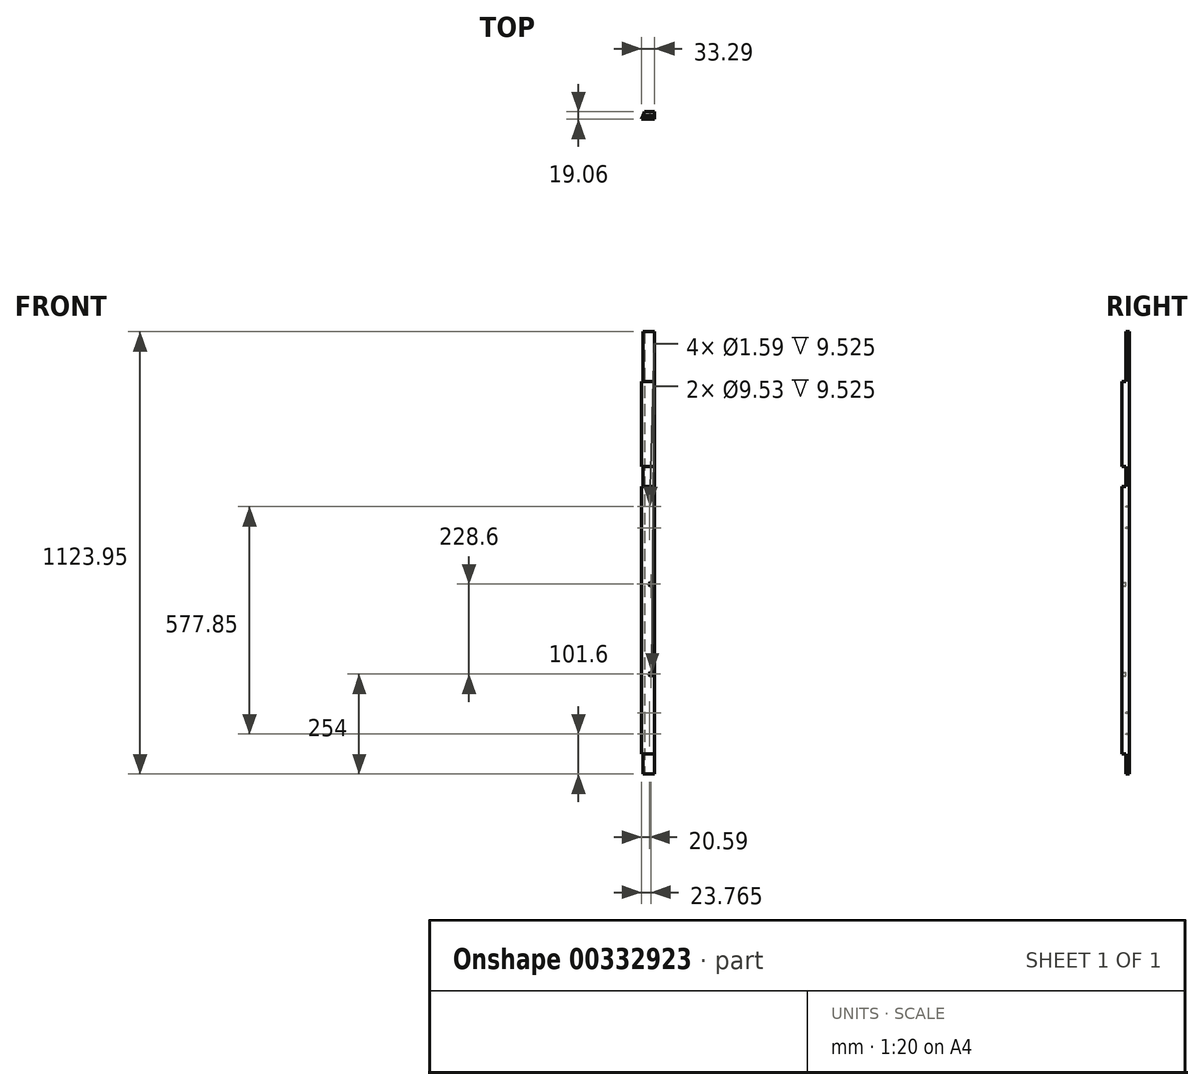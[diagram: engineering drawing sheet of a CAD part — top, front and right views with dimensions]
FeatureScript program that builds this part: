
annotation { "Feature Type Name" : "Feature", "Feature Type Description" : "" }
export const myFeature = defineFeature(function(context is Context, id is Id, definition is map)
    precondition{}
    {
        {
            var Q0;
            Q0=qCreatedBy(makeId("Top.planeOp"),FACE);
            var sketch = newSketch(context, id + "F0", { "sketchPlane" : qUnion([Q0])});
            skLineSegment(sketch, "E0.bottom", {"start": v(25.4, 9.53) * mm, "end": v(0, 9.53) * mm});
            skLineSegment(sketch, "E0.top", {"start": v(25.4, -9.53) * mm, "end": v(-7.9, -9.53) * mm});
            skLineSegment(sketch, "E0.left", {"start": v(25.4, 9.53) * mm, "end": v(25.4, -9.52) * mm});
            skPoint(sketch, "E0.middle", {"position": v(0, 0) * mm});
            skLineSegment(sketch, "E1", {"start": v(0, 9.53) * mm, "end": v(-7.9, -9.52) * mm});
            skPoint(sketch, "E0.right.end.orphan", {"position": v(-25.4, -9.53) * mm});
            skPoint(sketch, "E2.orphan", {"position": v(-25.4, 9.53) * mm});
            skSolve(sketch);
        }
        {
            var Q0;
            Q0=makeQuery(id+"F0.imprint","IMPRINT",FACE,{"disambiguationData":[TD([[makeQuery(id+"F0.imprint","IMPRINT",EDGE,{"derivedFrom":sQuery(id+"F0.wireOp",EDGE,"E0.bottom")}),1.0]])]});
            extrude(context, id + "F1", {"entities" : qUnion([Q0]), "depth" : 1123.95 * mm});
        }
        {
            var Q0;
            Q0=qCreatedBy(makeId("Front.planeOp"),FACE);
            var sketch = newSketch(context, id + "F2", { "sketchPlane" : qUnion([Q0])});
            skLineSegment(sketch, "E3.bottom", {"start": v(-38.77, 0) * mm, "end": v(83.66, 0) * mm});
            skLineSegment(sketch, "E3.top", {"start": v(-38.77, 50.8) * mm, "end": v(83.66, 50.8) * mm});
            skLineSegment(sketch, "E3.left", {"start": v(-38.77, 0) * mm, "end": v(-38.77, 50.8) * mm});
            skLineSegment(sketch, "E3.right", {"start": v(83.66, 0) * mm, "end": v(83.66, 50.8) * mm});
            skLineSegment(sketch, "E4.bottom", {"start": v(-44.21, 730.25) * mm, "end": v(49.65, 730.25) * mm});
            skLineSegment(sketch, "E4.top", {"start": v(-44.21, 781.05) * mm, "end": v(49.65, 781.05) * mm});
            skLineSegment(sketch, "E4.left", {"start": v(-44.21, 730.25) * mm, "end": v(-44.21, 781.05) * mm});
            skLineSegment(sketch, "E4.right", {"start": v(49.65, 730.25) * mm, "end": v(49.65, 781.05) * mm});
            skLineSegment(sketch, "E5.bottom", {"start": v(-210.36, 996.95) * mm, "end": v(132.8, 996.95) * mm});
            skLineSegment(sketch, "E5.top", {"start": v(-210.36, 1123.95) * mm, "end": v(132.8, 1123.95) * mm});
            skLineSegment(sketch, "E5.left", {"start": v(-210.36, 996.95) * mm, "end": v(-210.36, 1123.95) * mm});
            skLineSegment(sketch, "E5.right", {"start": v(132.8, 996.95) * mm, "end": v(132.8, 1123.95) * mm});
            skSolve(sketch);
        }
        {
            var Q0;
            Q0=qSketchRegion(id+"F2",true);
            extrude(context, id + "F3", {"entities" : qUnion([Q0]), "operationType" : NewBodyOperationType.REMOVE, "depth" : 25.4 * mm});
        }
        {
            var Q0;
            Q0=qCreatedBy(makeId("Front.planeOp"),FACE);
            var sketch = newSketch(context, id + "F4", { "sketchPlane" : qUnion([Q0])});
            skCircle(sketch, "E6", {"center": v(12.7, 101.6) * mm, "radius": 0.8 * mm});
            skCircle(sketch, "E7", {"center": v(12.7, 155.58) * mm, "radius": 0.8 * mm});
            skCircle(sketch, "E8", {"center": v(12.7, 625.48) * mm, "radius": 0.8 * mm});
            skCircle(sketch, "E9", {"center": v(12.7, 679.45) * mm, "radius": 0.8 * mm});
            skLineSegment(sketch, "E10", {"start": v(0, 0) * mm, "end": v(0, 1192.46) * mm, "construction": true});
            skLineSegment(sketch, "E11.bottom", {"start": v(12.7, 101.6) * mm, "end": v(-12.7, 101.6) * mm, "construction": true});
            skLineSegment(sketch, "E11.top", {"start": v(12.7, 679.45) * mm, "end": v(-12.7, 679.45) * mm, "construction": true});
            skLineSegment(sketch, "E11.left", {"start": v(12.7, 101.6) * mm, "end": v(12.7, 679.45) * mm, "construction": true});
            skLineSegment(sketch, "E11.right", {"start": v(-12.7, 101.6) * mm, "end": v(-12.7, 679.45) * mm, "construction": true});
            skCircle(sketch, "E12", {"center": v(-12.7, 625.48) * mm, "radius": 0.8 * mm});
            skCircle(sketch, "E13", {"center": v(-12.7, 679.45) * mm, "radius": 0.8 * mm});
            skCircle(sketch, "E14", {"center": v(-12.7, 101.6) * mm, "radius": 0.8 * mm});
            skCircle(sketch, "E15", {"center": v(-12.7, 155.58) * mm, "radius": 0.8 * mm});
            skSolve(sketch);
        }
        {
            var Q0;
            Q0=qSketchRegion(id+"F4",true);
            extrude(context, id + "F5", {"entities" : qUnion([Q0]), "operationType" : NewBodyOperationType.REMOVE, "oppositeDirection" : true, "depth" : 25.4 * mm});
        }
        {
            var Q0;
            Q0=qCreatedBy(makeId("Front.planeOp"),FACE);
            var sketch = newSketch(context, id + "F6", { "sketchPlane" : qUnion([Q0])});
            skCircle(sketch, "E16", {"center": v(15.88, 254) * mm, "radius": 4.76 * mm});
            skCircle(sketch, "E17", {"center": v(15.87, 482.6) * mm, "radius": 4.76 * mm});
            skSolve(sketch);
        }
        {
            var Q0;
            Q0 = qSketchRegion(id + "F6", true);
            extrude(context, id + "F7", {"entities" : qUnion([Q0]), "operationType" : NewBodyOperationType.REMOVE, "depth" : 25.4 * mm});
        }
    });
